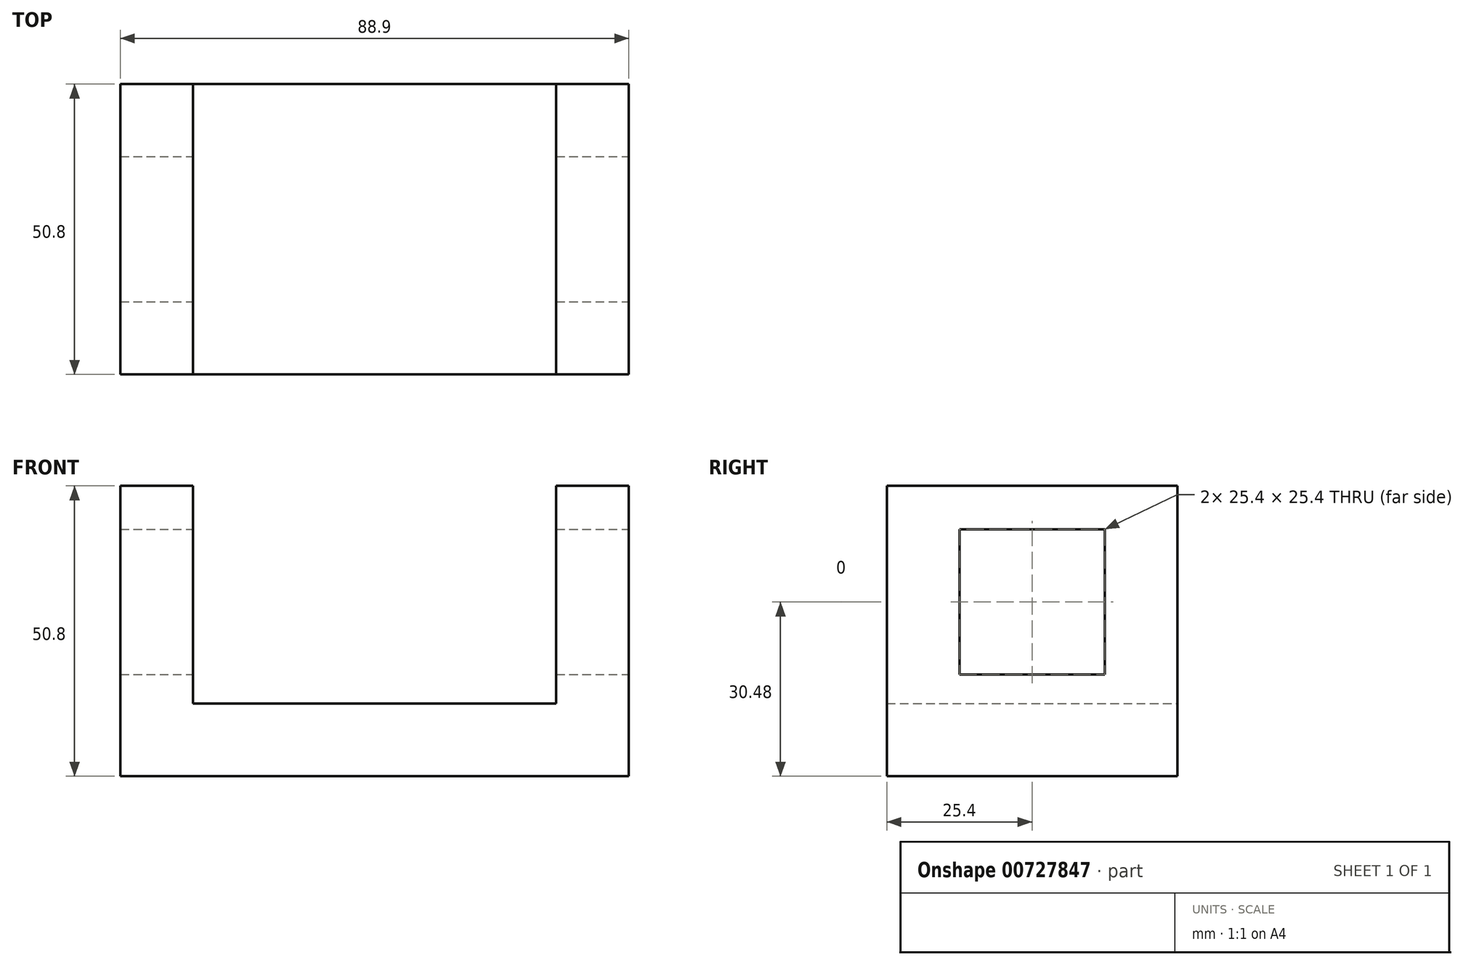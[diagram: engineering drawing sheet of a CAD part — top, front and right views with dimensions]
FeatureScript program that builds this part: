
annotation { "Feature Type Name" : "Feature", "Feature Type Description" : "" }
export const myFeature = defineFeature(function(context is Context, id is Id, definition is map)
    precondition{}
    {
        {
            var Q0;
            Q0=qCreatedBy(makeId("Front.planeOp"),FACE);
            var sketch = newSketch(context, id + "F0", { "sketchPlane" : qUnion([Q0])});
            skLineSegment(sketch, "E0", {"start": v(-28.17, 50.8) * mm, "end": v(-15.47, 50.8) * mm});
            skLineSegment(sketch, "E1", {"start": v(-15.47, 50.8) * mm, "end": v(-15.47, 12.7) * mm});
            skLineSegment(sketch, "E2", {"start": v(-15.47, 12.7) * mm, "end": v(48.03, 12.7) * mm});
            skLineSegment(sketch, "E3", {"start": v(48.03, 12.7) * mm, "end": v(48.03, 50.8) * mm});
            skLineSegment(sketch, "E4", {"start": v(48.03, 50.8) * mm, "end": v(60.73, 50.8) * mm});
            skLineSegment(sketch, "E5", {"start": v(60.73, 50.8) * mm, "end": v(60.73, 0) * mm});
            skLineSegment(sketch, "E6", {"start": v(60.73, 0) * mm, "end": v(-28.17, 0) * mm});
            skLineSegment(sketch, "E7", {"start": v(-28.17, 0) * mm, "end": v(-28.17, 50.8) * mm});
            skSolve(sketch);
        }
        {
            var Q0;
            Q0=makeQuery(id+"F0.imprint","IMPRINT",FACE,{"disambiguationData":[TD([[makeQuery(id+"F0.imprint","IMPRINT",EDGE,{"derivedFrom":sQuery(id+"F0.wireOp",EDGE,"E0")}),-1.0]])]});
            extrude(context, id + "F1", {"entities" : qUnion([Q0]), "depth" : 50.8 * mm, "offsetDistance" : 25.4 * mm});
        }
        {
            var Q0;
            Q0=makeQuery(id+"F1.opExtrude","SWEPT_FACE",FACE,{"disambiguationData":[OSD([sQuery(id+"F0.wireOp",EDGE,"E5")])]});
            var sketch = newSketch(context, id + "F2", { "sketchPlane" : qUnion([Q0])});
            skLineSegment(sketch, "E8.bottom", {"start": v(-12.7, 43.18) * mm, "end": v(-38.1, 43.18) * mm});
            skLineSegment(sketch, "E8.top", {"start": v(-12.7, 17.78) * mm, "end": v(-38.1, 17.78) * mm});
            skLineSegment(sketch, "E8.left", {"start": v(-12.7, 43.18) * mm, "end": v(-12.7, 17.78) * mm});
            skLineSegment(sketch, "E8.right", {"start": v(-38.1, 43.18) * mm, "end": v(-38.1, 17.78) * mm});
            skPoint(sketch, "E8.middle", {"position": v(-25.4, 30.48) * mm});
            skSolve(sketch);
        }
        {
            var Q0;
            Q0=makeQuery(id+"F2.imprint","IMPRINT",FACE,{"disambiguationData":[TD([[makeQuery(id+"F2.imprint","IMPRINT",EDGE,{"derivedFrom":sQuery(id+"F2.wireOp",EDGE,"E8.bottom")}),1.0]])]});
            extrude(context, id + "F3", {"entities" : qUnion([Q0]), "operationType" : NewBodyOperationType.REMOVE, "oppositeDirection" : true, "depth" : 127 * mm, "offsetDistance" : 25.4 * mm});
        }
    });
